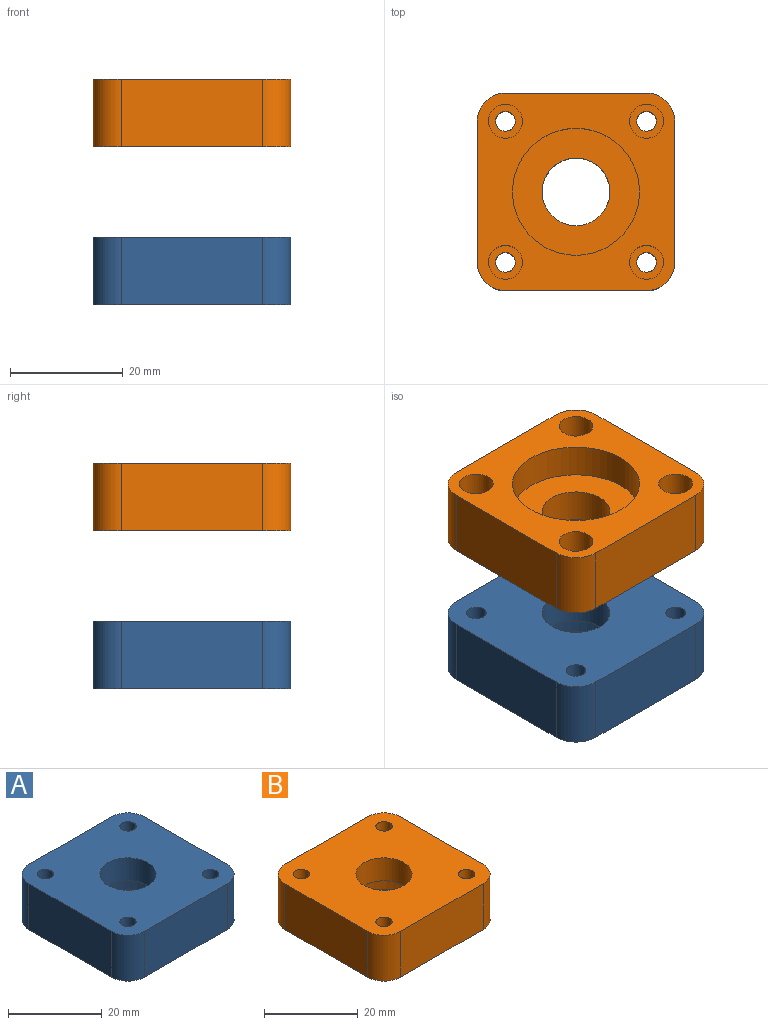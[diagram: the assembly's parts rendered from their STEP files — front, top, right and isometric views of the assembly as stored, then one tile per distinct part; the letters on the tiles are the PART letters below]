
ASSEMBLY  parts=2 mates=1
PART A: 45 faces, bbox 35x35x12 mm
  f0: plane 35x35mm, normal (0,0,-1), area 691.4mm2, adj f1,f2,f3,f8,f11,f13,f14,f15
  f1: plane 25x12mm, normal (0,1,0), area 300mm2, adj f0,f10,f41,f44
  f2: plane 25x12mm, normal (-1,0,0), area 300mm2, adj f0,f10,f41,f42
  f3: plane 25x12mm, normal (0,-1,0), area 300mm2, adj f0,f10,f42,f43
  f4: cylinder r=1.75mm len=6mm, axis (0,0,-1), area 66mm2, adj f10,f33
  f5: cylinder r=1.75mm len=6mm, axis (0,0,-1), area 66mm2, adj f10,f19
  f6: cylinder r=1.75mm len=6mm, axis (0,0,-1), area 66mm2, adj f10,f40
  f7: cylinder r=1.75mm len=6mm, axis (0,0,-1), area 66mm2, adj f10,f26
  f8: plane 25x12mm, normal (1,0,0), area 300mm2, adj f0,f10,f43,f44
  f9: cylinder r=6mm len=12mm, axis (0,0,-1), area 226.2mm2, adj f10,f12
  f10: plane 35x35mm, normal (0,0,1), area 1052mm2, adj f1,f2,f3,f4,f5,f6,f7,f8
  f11: cylinder r=11.25mm len=22.5mm, axis (0,0,-1), area 424.1mm2, adj f0,f12
  f12: plane 22.5x22.5mm, normal (0,0,-1), area 284.5mm2, adj f9,f11
  f13: plane 6x3.32mm, normal (0,-1,0), area 19.9mm2, adj f0,f14,f18,f19
  f14: plane 6x2.88mm, normal (0.87,-0.5,0), area 19.9mm2, adj f0,f13,f15,f19
  f15: plane 6x2.88mm, normal (0.87,0.5,0), area 19.9mm2, adj f0,f14,f16,f19
  f16: plane 6x3.32mm, normal (0,1,0), area 19.9mm2, adj f0,f15,f17,f19
  f17: plane 6x2.88mm, normal (-0.87,0.5,0), area 19.9mm2, adj f0,f16,f18,f19
  f18: plane 6x2.88mm, normal (-0.87,-0.5,0), area 19.9mm2, adj f0,f13,f17,f19
  f19: plane 6.64x5.75mm, normal (0,0,-1), area 19mm2, adj f5,f13,f14,f15,f16,f17,f18
  f20: plane 6x2.88mm, normal (-0.87,0.5,0), area 19.9mm2, adj f0,f21,f25,f26
  f21: plane 6x2.88mm, normal (-0.87,-0.5,0), area 19.9mm2, adj f0,f20,f22,f26
  f22: plane 6x3.32mm, normal (0,-1,0), area 19.9mm2, adj f0,f21,f23,f26
  f23: plane 6x2.88mm, normal (0.87,-0.5,0), area 19.9mm2, adj f0,f22,f24,f26
  f24: plane 6x2.88mm, normal (0.87,0.5,0), area 19.9mm2, adj f0,f23,f25,f26
  f25: plane 6x3.32mm, normal (0,1,0), area 19.9mm2, adj f0,f20,f24,f26
  f26: plane 6.64x5.75mm, normal (0,0,-1), area 19mm2, adj f7,f20,f21,f22,f23,f24,f25
  f27: plane 6x3.32mm, normal (0,-1,0), area 19.9mm2, adj f0,f28,f32,f33
  f28: plane 6x2.88mm, normal (0.87,-0.5,0), area 19.9mm2, adj f0,f27,f29,f33
  f29: plane 6x2.88mm, normal (0.87,0.5,0), area 19.9mm2, adj f0,f28,f30,f33
  f30: plane 6x3.32mm, normal (0,1,0), area 19.9mm2, adj f0,f29,f31,f33
  f31: plane 6x2.88mm, normal (-0.87,0.5,0), area 19.9mm2, adj f0,f30,f32,f33
  f32: plane 6x2.88mm, normal (-0.87,-0.5,0), area 19.9mm2, adj f0,f27,f31,f33
  f33: plane 6.64x5.75mm, normal (0,0,-1), area 19mm2, adj f4,f27,f28,f29,f30,f31,f32
  f34: plane 6x2.88mm, normal (0.87,-0.5,0), area 19.9mm2, adj f0,f35,f39,f40
  f35: plane 6x2.88mm, normal (0.87,0.5,0), area 19.9mm2, adj f0,f34,f36,f40
  f36: plane 6x3.32mm, normal (0,1,0), area 19.9mm2, adj f0,f35,f37,f40
  f37: plane 6x2.88mm, normal (-0.87,0.5,0), area 19.9mm2, adj f0,f36,f38,f40
  f38: plane 6x2.88mm, normal (-0.87,-0.5,0), area 19.9mm2, adj f0,f37,f39,f40
  f39: plane 6x3.32mm, normal (0,-1,0), area 19.9mm2, adj f0,f34,f38,f40
  f40: plane 6.64x5.75mm, normal (0,0,-1), area 19mm2, adj f6,f34,f35,f36,f37,f38,f39
  f41: cylinder r=5mm len=12mm, axis (0,0,1), area 94.2mm2, adj f0,f1,f2,f10
  f42: cylinder r=5mm len=12mm, axis (0,0,-1), area 94.2mm2, adj f0,f2,f3,f10
  f43: cylinder r=5mm len=12mm, axis (0,0,1), area 94.2mm2, adj f0,f3,f8,f10
  f44: cylinder r=5mm len=12mm, axis (0,0,-1), area 94.2mm2, adj f0,f1,f8,f10
PART B: 25 faces, bbox 35x35x12 mm
  f0: plane 25x12mm, normal (0,1,0), area 300mm2, adj f9,f10,f21,f24
  f1: plane 25x12mm, normal (-1,0,0), area 300mm2, adj f9,f10,f21,f22
  f2: plane 25x12mm, normal (0,-1,0), area 300mm2, adj f9,f10,f22,f23
  f3: cylinder r=1.75mm len=6mm, axis (0,0,-1), area 66mm2, adj f9,f14
  f4: cylinder r=1.75mm len=6mm, axis (0,0,-1), area 66mm2, adj f9,f16
  f5: cylinder r=6mm len=12mm, axis (0,0,-1), area 226.2mm2, adj f9,f12
  f6: plane 25x12mm, normal (1,0,0), area 300mm2, adj f9,f10,f23,f24
  f7: cylinder r=1.75mm len=6mm, axis (0,0,-1), area 66mm2, adj f9,f18
  f8: cylinder r=1.75mm len=6mm, axis (0,0,-1), area 66mm2, adj f9,f20
  f9: plane 35x35mm, normal (0,0,1), area 1052mm2, adj f0,f1,f2,f3,f4,f5,f6,f7
  f10: plane 35x35mm, normal (0,0,-1), area 692.8mm2, adj f0,f1,f2,f6,f11,f13,f15,f17
  f11: cylinder r=11.25mm len=22.5mm, axis (0,0,-1), area 424.1mm2, adj f10,f12
  f12: plane 22.5x22.5mm, normal (0,0,-1), area 284.5mm2, adj f5,f11
  f13: cylinder r=3mm len=6mm, axis (0,0,-1), area 113.1mm2, adj f10,f14
  f14: plane 6x6mm, normal (0,0,-1), area 18.7mm2, adj f3,f13
  f15: cylinder r=3mm len=6mm, axis (0,0,-1), area 113.1mm2, adj f10,f16
  f16: plane 6x6mm, normal (0,0,-1), area 18.7mm2, adj f4,f15
  f17: cylinder r=3mm len=6mm, axis (0,0,-1), area 113.1mm2, adj f10,f18
  f18: plane 6x6mm, normal (0,0,-1), area 18.7mm2, adj f7,f17
  f19: cylinder r=3mm len=6mm, axis (0,0,-1), area 113.1mm2, adj f10,f20
  f20: plane 6x6mm, normal (0,0,-1), area 18.7mm2, adj f8,f19
  f21: cylinder r=5mm len=12mm, axis (0,0,1), area 94.2mm2, adj f0,f1,f9,f10
  f22: cylinder r=5mm len=12mm, axis (0,0,-1), area 94.2mm2, adj f1,f2,f9,f10
  f23: cylinder r=5mm len=12mm, axis (0,0,1), area 94.2mm2, adj f2,f6,f9,f10
  f24: cylinder r=5mm len=12mm, axis (0,0,-1), area 94.2mm2, adj f0,f6,f9,f10
PLACE A t=(-60.42,22.69,5.47)mm
PLACE B rot(axis=(0.71,-0.71,0),180deg) t=(-60.42,22.69,45.47)mm
MATE fastened A.f7 <-> B.f7  axis (0,0,1) through (-72.92,35.19,17.47)mm
